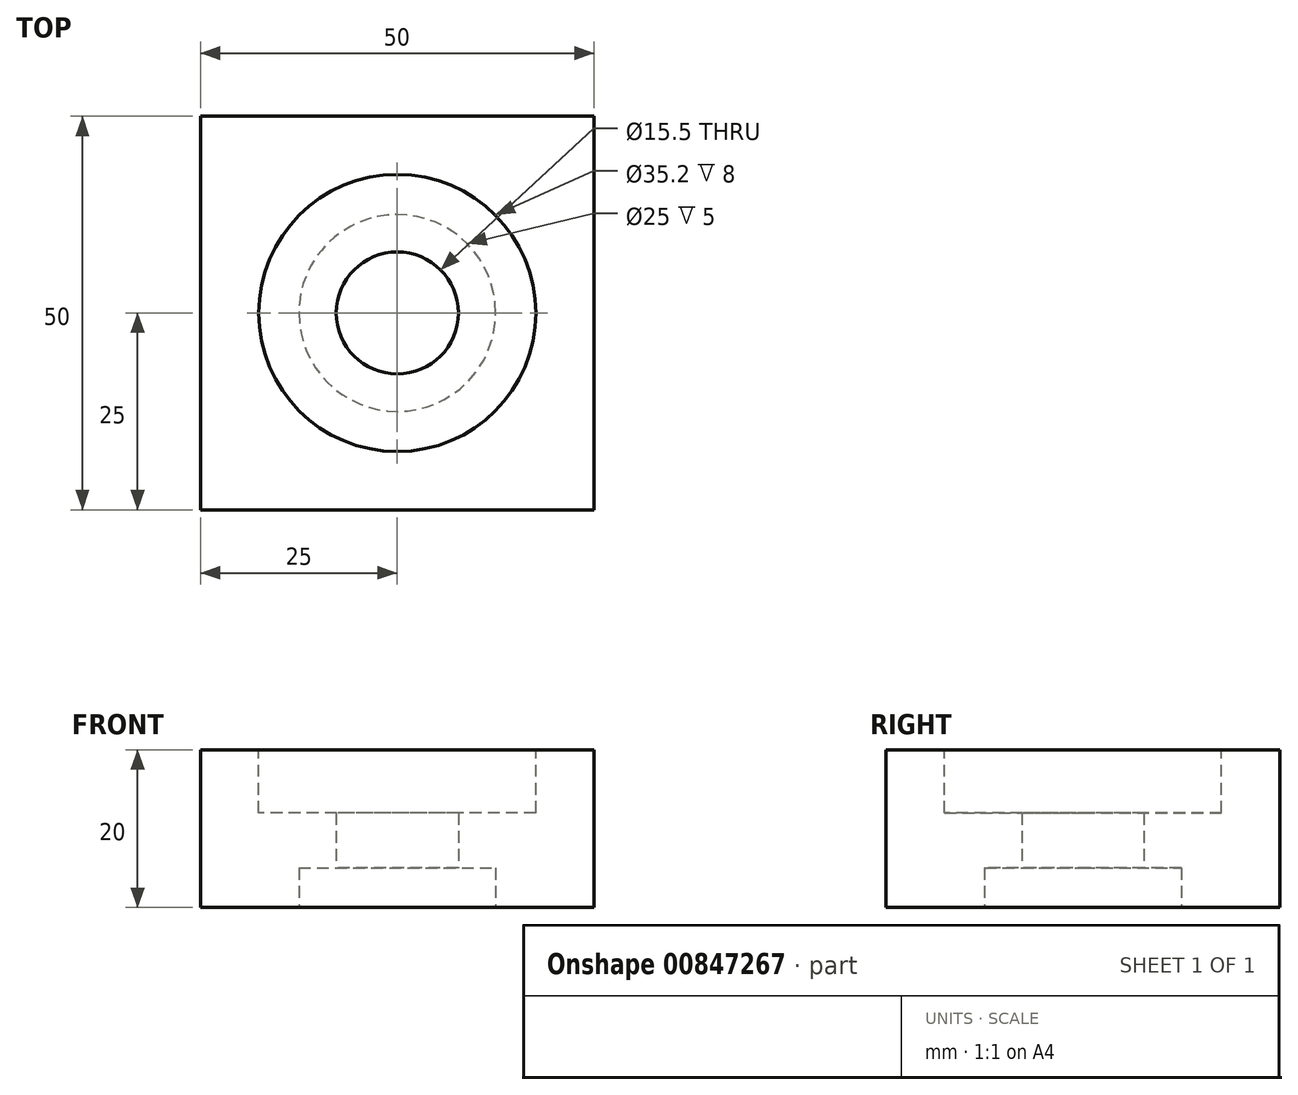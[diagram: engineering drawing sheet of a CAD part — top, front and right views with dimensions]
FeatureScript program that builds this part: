
annotation { "Feature Type Name" : "Feature", "Feature Type Description" : "" }
export const myFeature = defineFeature(function(context is Context, id is Id, definition is map)
    precondition{}
    {
        {
            var Q0;
            Q0=qCreatedBy(makeId("Top.planeOp"),FACE);
            var sketch = newSketch(context, id + "F0", { "sketchPlane" : qUnion([Q0])});
            skLineSegment(sketch, "E0.bottom", {"start": v(-25, 25) * mm, "end": v(25, 25) * mm});
            skLineSegment(sketch, "E0.top", {"start": v(-25, -25) * mm, "end": v(25, -25) * mm});
            skLineSegment(sketch, "E0.left", {"start": v(-25, 25) * mm, "end": v(-25, -25) * mm});
            skLineSegment(sketch, "E0.right", {"start": v(25, 25) * mm, "end": v(25, -25) * mm});
            skPoint(sketch, "E0.middle", {"position": v(0, 0) * mm});
            skCircle(sketch, "E1", {"center": v(0, 0) * mm, "radius": 7.75 * mm});
            skSolve(sketch);
        }
        {
            var Q0;
            Q0=makeQuery(id+"F0.imprint","IMPRINT",FACE,{"disambiguationData":[TD([[makeQuery(id+"F0.imprint","IMPRINT",EDGE,{"derivedFrom":sQuery(id+"F0.wireOp",EDGE,"E0.bottom")}),-1.0]])]});
            extrude(context, id + "F1", {"entities" : qUnion([Q0]), "depth" : 20 * mm, "offsetDistance" : 25 * mm});
        }
        {
            var Q0;
            Q0=makeQuery(id+"F1.opExtrude","CAP_FACE",FACE,{"disambiguationData":[OSD([sQuery(id+"F0.wireOp",EDGE,"E0.bottom"),sQuery(id+"F0.wireOp",EDGE,"E0.top"),sQuery(id+"F0.wireOp",EDGE,"E0.left"),sQuery(id+"F0.wireOp",EDGE,"E0.right"),sQuery(id+"F0.wireOp",EDGE,"E1")])],"isStart":false});
            var sketch = newSketch(context, id + "F2", { "sketchPlane" : qUnion([Q0])});
            skCircle(sketch, "E2", {"center": v(0, 0) * mm, "radius": 17.6 * mm});
            skSolve(sketch);
        }
        {
            var Q0;
            Q0=makeQuery(id+"F2.imprint","IMPRINT",FACE,{"disambiguationData":[TD([[makeQuery(id+"F2.imprint","IMPRINT",EDGE,{"derivedFrom":sQuery(id+"F2.wireOp",EDGE,"E2")}),1.0]])]});
            extrude(context, id + "F3", {"entities" : qUnion([Q0]), "operationType" : NewBodyOperationType.REMOVE, "oppositeDirection" : true, "depth" : 8 * mm, "offsetDistance" : 25 * mm});
        }
        {
            var Q0;
            Q0=makeQuery(id+"F1.opExtrude","CAP_FACE",FACE,{"disambiguationData":[OSD([sQuery(id+"F0.wireOp",EDGE,"E0.bottom"),sQuery(id+"F0.wireOp",EDGE,"E0.top"),sQuery(id+"F0.wireOp",EDGE,"E0.left"),sQuery(id+"F0.wireOp",EDGE,"E0.right"),sQuery(id+"F0.wireOp",EDGE,"E1")])],"isStart":true});
            var sketch = newSketch(context, id + "F4", { "sketchPlane" : qUnion([Q0])});
            skCircle(sketch, "E3", {"center": v(0, 0) * mm, "radius": 12.5 * mm});
            skSolve(sketch);
        }
        {
            var Q0;
            Q0=makeQuery(id+"F4.imprint","IMPRINT",FACE,{"disambiguationData":[TD([[makeQuery(id+"F4.imprint","IMPRINT",EDGE,{"derivedFrom":sQuery(id+"F4.wireOp",EDGE,"E3")}),1.0]])]});
            extrude(context, id + "F5", {"entities" : qUnion([Q0]), "operationType" : NewBodyOperationType.REMOVE, "oppositeDirection" : true, "depth" : 5 * mm, "offsetDistance" : 25 * mm});
        }
    });
